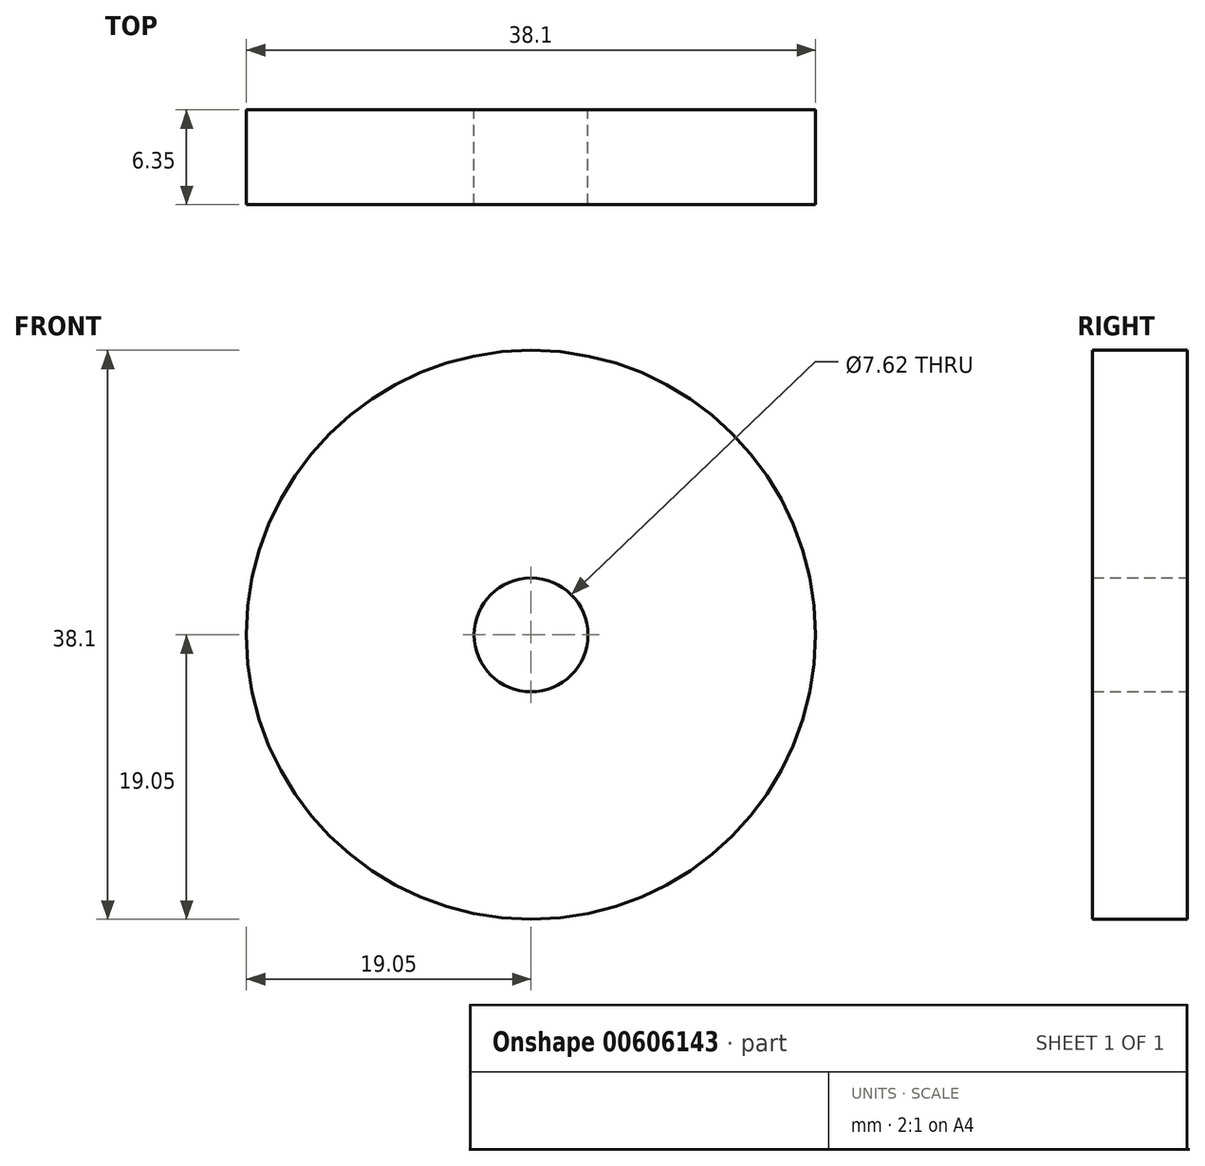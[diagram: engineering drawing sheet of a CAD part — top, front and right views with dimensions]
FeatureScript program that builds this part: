
annotation { "Feature Type Name" : "Feature", "Feature Type Description" : "" }
export const myFeature = defineFeature(function(context is Context, id is Id, definition is map)
    precondition{}
    {
        {
            var Q0;
            Q0=qCreatedBy(makeId("Front.planeOp"),FACE);
            var sketch = newSketch(context, id + "F0", { "sketchPlane" : qUnion([Q0])});
            skCircle(sketch, "E0", {"center": v(0, 0) * mm, "radius": 19.05 * mm});
            skCircle(sketch, "E1", {"center": v(0, 0) * mm, "radius": 3.81 * mm});
            skSolve(sketch);
        }
        {
            var Q0;
            Q0=makeQuery(id+"F0.imprint","IMPRINT",FACE,{"disambiguationData":[TD([[makeQuery(id+"F0.imprint","IMPRINT",EDGE,{"derivedFrom":sQuery(id+"F0.wireOp",EDGE,"E0")}),1.0]])]});
            extrude(context, id + "F1", {"entities" : qUnion([Q0]), "depth" : 6.35 * mm, "offsetDistance" : 25.4 * mm});
        }
    });
